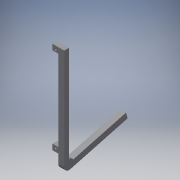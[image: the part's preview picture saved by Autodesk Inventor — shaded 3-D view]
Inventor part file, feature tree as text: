
AUTODESK INVENTOR PART (.ipt)
format: ipt  version: 2018 (Build 220112000, 112)  size: 135,680 bytes
history: native  units: in
note: dims shown in document units (in); Inventor stores cm internally (conversion verified against a paired STEP export)
features: extrude x2, sketch x2
ambient origin geometry x8: Origin, YZ Plane, XZ Plane, XY Plane, X Axis, Y Axis, Z Axis, Center Point
bodies: Body1 (feature_tree)
feature tree (4):
  extrude  "Extrusion3"  Depth=0.315in
  extrude  "Extrusion4"  Depth=0.315in
  sketch  "Sketch1"  dims[d0=4.8925in d1=0.315in]
  sketch  "Sketch4"  dims[d2=0.122in d3=0.122in d4=4.526in d5=0.1181in d6=3.0886in d7=0.315in d17=0.2559in d18=0.0in d19=0.4724in d20=75.0deg d21=0.315in d22=3.1496in d23=0.2756in d24=0.0in]
